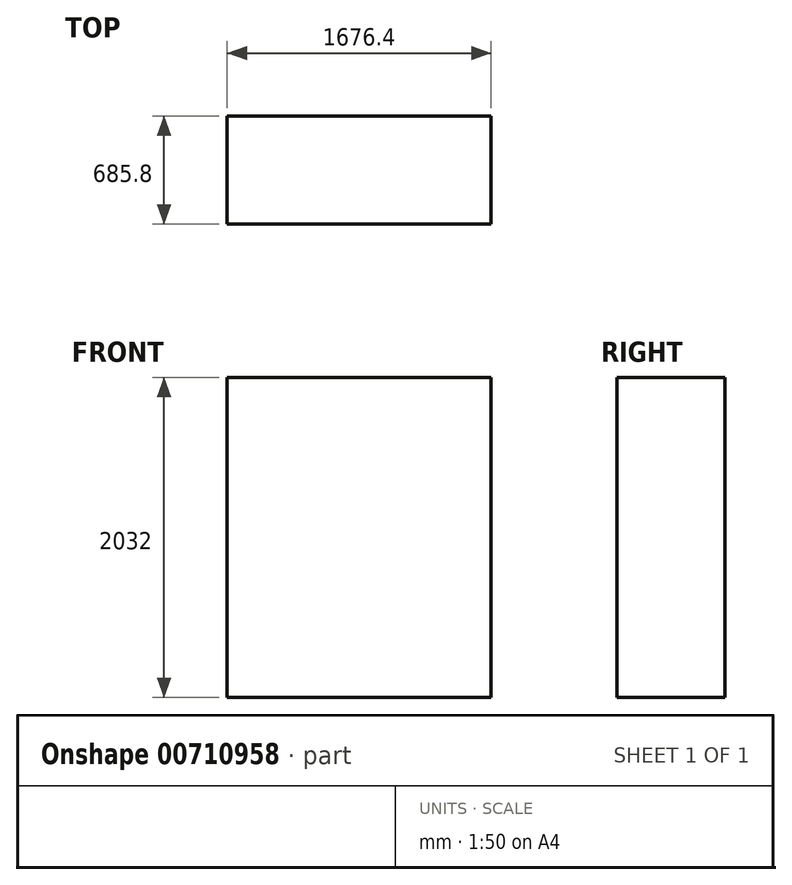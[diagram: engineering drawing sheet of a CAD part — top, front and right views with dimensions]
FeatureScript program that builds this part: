
annotation { "Feature Type Name" : "Feature", "Feature Type Description" : "" }
export const myFeature = defineFeature(function(context is Context, id is Id, definition is map)
    precondition{}
    {
        {
            var Q0;
            Q0=qCreatedBy(makeId("Top.planeOp"),FACE);
            var sketch = newSketch(context, id + "F0", { "sketchPlane" : qUnion([Q0])});
            skLineSegment(sketch, "E0.bottom", {"start": v(-983.02, -1225) * mm, "end": v(693.38, -1225) * mm});
            skLineSegment(sketch, "E0.top", {"start": v(-983.02, -539.2) * mm, "end": v(693.38, -539.2) * mm});
            skLineSegment(sketch, "E0.left", {"start": v(-983.02, -1225) * mm, "end": v(-983.02, -539.2) * mm});
            skLineSegment(sketch, "E0.right", {"start": v(693.38, -1225) * mm, "end": v(693.38, -539.2) * mm});
            skSolve(sketch);
        }
        {
            var Q0;
            Q0 = qSketchRegion(id + "F0", true);
            extrude(context, id + "F1", {"entities" : qUnion([Q0]), "depth" : 2032 * mm, "offsetDistance" : 25.4 * mm});
        }
    });
